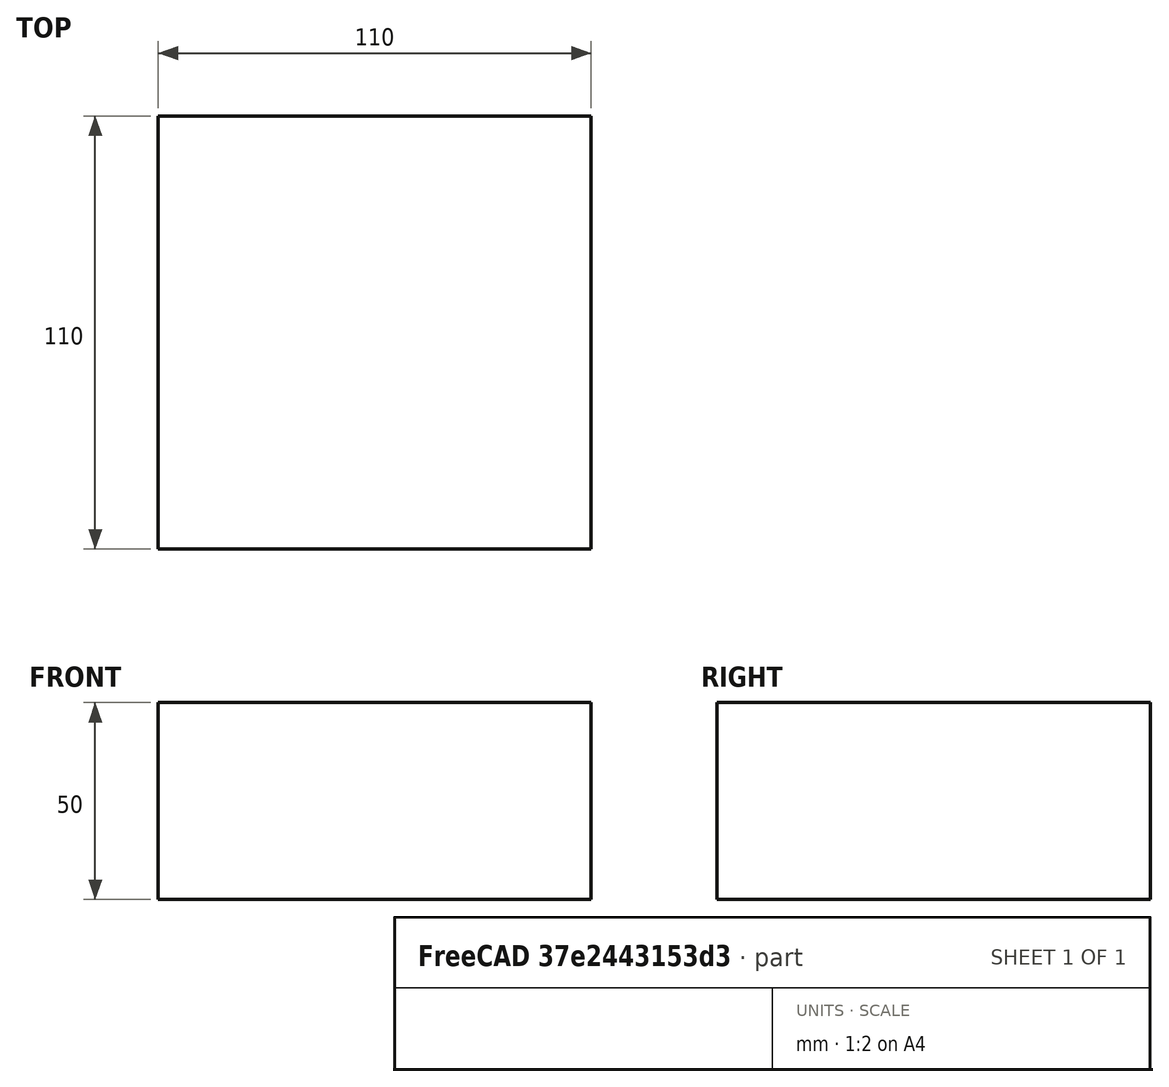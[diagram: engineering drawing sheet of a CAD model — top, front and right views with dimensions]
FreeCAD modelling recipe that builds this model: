
FCSTD DOCUMENT  (FreeCAD 0.15R4671 (Git))
Label: Square Bar 110 EN10059 S235JR
License: All rights reserved
LicenseURL: http://en.wikipedia.org/wiki/All_rights_reserved
objects: Sketcher::SketchObject×1, Part::Extrusion×1
note: 2 computed .brp shape members not serialized (recipe doc carries the construction recipe); baked Part::Feature solids carry a one-line shape summary decoded from their .brp

FEATURE [Sketcher::SketchObject] Sketch
  sketch-geometry (4):
    g0: LineSegment StartX=-55 StartY=-55 StartZ=0 EndX=55 EndY=-55 EndZ=0
    g1: LineSegment StartX=55 StartY=-55 StartZ=0 EndX=55 EndY=55 EndZ=0
    g2: LineSegment StartX=55 StartY=55 StartZ=0 EndX=-55 EndY=55 EndZ=0
    g3: LineSegment StartX=-55 StartY=55 StartZ=0 EndX=-55 EndY=-55 EndZ=0
  constraints (12):
    c: Coincident(g0,g1)
    c: Coincident(g1,g2)
    c: Coincident(g2,g3)
    c: Coincident(g3,g0)
    c: Horizontal(g0)
    c: Horizontal(g2)
    c: Vertical(g1)
    c: Vertical(g3)
    c: Symmetric(g1,g0,g-1)
    c: Symmetric(g2,g1,g-2)
    c: Equal(g1,g2)
    c: DistanceY(g1) = 110
FEATURE [Part::Extrusion] Extrude  label="Square Bar 110 EN10059 S235JR"
  Base = -> Sketch
  Dir = (0,0,50)
  Solid = true
